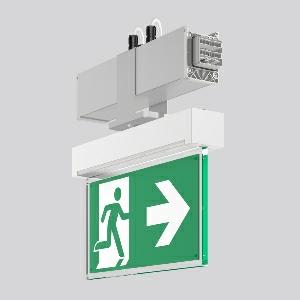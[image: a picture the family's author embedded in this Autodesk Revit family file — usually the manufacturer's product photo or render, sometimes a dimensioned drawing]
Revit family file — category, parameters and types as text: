
# Revit family: linedo_module_rz_9503rz_760_430_030_e028
name_source: partatom
category: Lighting Fixtures
units: mm (PartAtom-declared; Revit-internal decimal feet)

## family parameters
Cut with Voids When Loaded = No
Host = Face
Light Source = No
Part Type = Normal
Room Calculation Point = No
Round Connector Dimension = Use Diameter
Shared = No

## types (1)
- LINEDO Module RZ
    Apparent Load = 0 VA
    Default Elevation = 1800 mm
    Description = LINEDO, silver, on/off
Continuous line luminaire, L 336 B 62 H 343, SBS, 3 h, automatischer Selbsttest
    Height = 343 mm
    Lamp = 0 x
    Length = 336 mm
    Luminous efficacy = 0 lm/W
    Manufacturer = RZB
    ModVariant = No
    Model = 9503RZ.760.430.030
    Mounting Place = Ceiling
    Mounting Type = Surface mounted
    Number of Poles = 1
    OnlyDefault = Yes
    Power Factor = 1
    Product Name = LINEDO Module RZ
    Product group = Continuous line luminaire system Linedo IP 54
    ProductGroupID = 314
    Protection Class = Protection class I
    Protection Degree = IP 54
    RLX_Detail_Level = 1
    RLX_Emergency_Light_Flux = 0 lm
    RLX_Emergency_Type = 0
    RLX_Emergency_Type_DB = No
    RlxData = <blob elided: 37417 chars, md5=8cf7c8a7>
    Standby Power = 0 W
    System Light Flux = 0 lm
    System Power = 0 W
    Type Comments = Product without accessories
    Type Image = 9503rz.760.434.030.jpg
    URL = http://relux.com
    VarID = ---
    Voltage = 0 V
    Weight = 0.00 kg
    Width = 62 mm  [stored 0.203412 ft]

note: [stored X ft] marks values corroborated as IEEE doubles in the binary element streams (Revit-internal decimal feet)

## geometry (parser evidence)
native form markers: Blend x4, Sweep x11
no freeform markers — native parametric forms only
